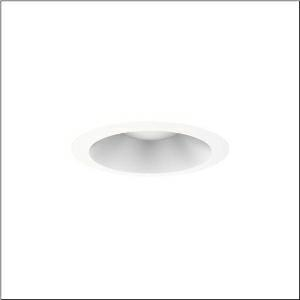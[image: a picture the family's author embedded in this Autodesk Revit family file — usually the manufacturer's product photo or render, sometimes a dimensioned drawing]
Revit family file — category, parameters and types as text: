
# Revit family: lunis_31_midi_51dn157g42
name_source: partatom
category: Lighting Fixtures
units: mm (PartAtom-declared; Revit-internal decimal feet)

## family parameters
Cut with Voids When Loaded = No
Host = Face
Light Source = No
Part Type = Normal
Room Calculation Point = No
Round Connector Dimension = Use Diameter
Shared = No

## types (1)
- Lunis 31 midi (1 x LED, 2150 lm, 17 W, 4000K)
    Apparent Load = 17 VA
    CIE Flux Codes = 89 99 100 100 100
    Color Rendering = 80
    Color Temperature = 4000K
    Default Elevation = 1800 mm
    Description = Lunis 31,  midi, downlight, light control with reflector, light emission: direct distribution, LED rated luminous flux: 2.150lm, light colour: 840, control gear: ECG, mains connection: 220..240V, AC, 50/60Hz, housing, white, protection rating (complete): IP20, insulation class (complete): insulation class II (safety insulation), certification: CE, packaging unit: 1 piece
    Height = 0 mm  [stored 0 ft]
    Lamp = 1 x LED
    Lamp Light Flux = 2150 lm
    Lamp Power = 17 W
    Lamp count = 1
    Length = 259 mm
    Luminous efficacy = 126 lm/W
    Manufacturer = Siteco
    ModVariant = No
    Model = 51DN157G42
    Mounting Place = Ceiling
    Mounting Type = Recessed
    Number of Poles = 1
    OnlyDefault = Yes
    Power Factor = 1
    Product Name = Lunis 31 midi
    Product group = downlight | ceiling recessed
    ProductGroupID = 402
    Protection Class = Protection class II
    Protection Degree = IP 20
    RLX_Detail_Level = 1
    RlxData = <blob elided: 23737 chars, md5=9212c326>
    Socket = socket
    Standby Power = 0 W
    System Light Flux = 2150 lm
    System Power = 17 W
    Type Comments = Product without accessories
    Type Image = l_1006711.jpg
    URL = http://relux.com
    VarID = ---
    Voltage = 0 V
    Weight = 0.00 kg
    Width = 0 mm  [stored 0 ft]

note: [stored X ft] marks values corroborated as IEEE doubles in the binary element streams (Revit-internal decimal feet)

## geometry (parser evidence)
native form markers: Blend x4, Sweep x10
no freeform markers — native parametric forms only
